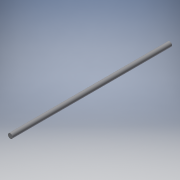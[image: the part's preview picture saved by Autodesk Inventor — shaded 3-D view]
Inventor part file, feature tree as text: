
AUTODESK INVENTOR PART (.ipt)
format: ipt  version: 2016 (Build 200138000, 138)  size: 87,552 bytes
history: native  units: in
note: dims shown in document units (in); Inventor stores cm internally (conversion verified against a paired STEP export)
features: extrude x1, sketch x1
ambient origin geometry x8: Origin, YZ Plane, XZ Plane, XY Plane, X Axis, Y Axis, Z Axis, Center Point
bodies: Solid1 (feature_tree)
feature tree (2):
  extrude  "Extrusion1"  Depth=5.0in TaperAngle=0.0deg
  sketch  "Sketch1"  dims[d0=0.188in d1=5.0in d2=0.0in d3=2.4in d4=0.0in]
